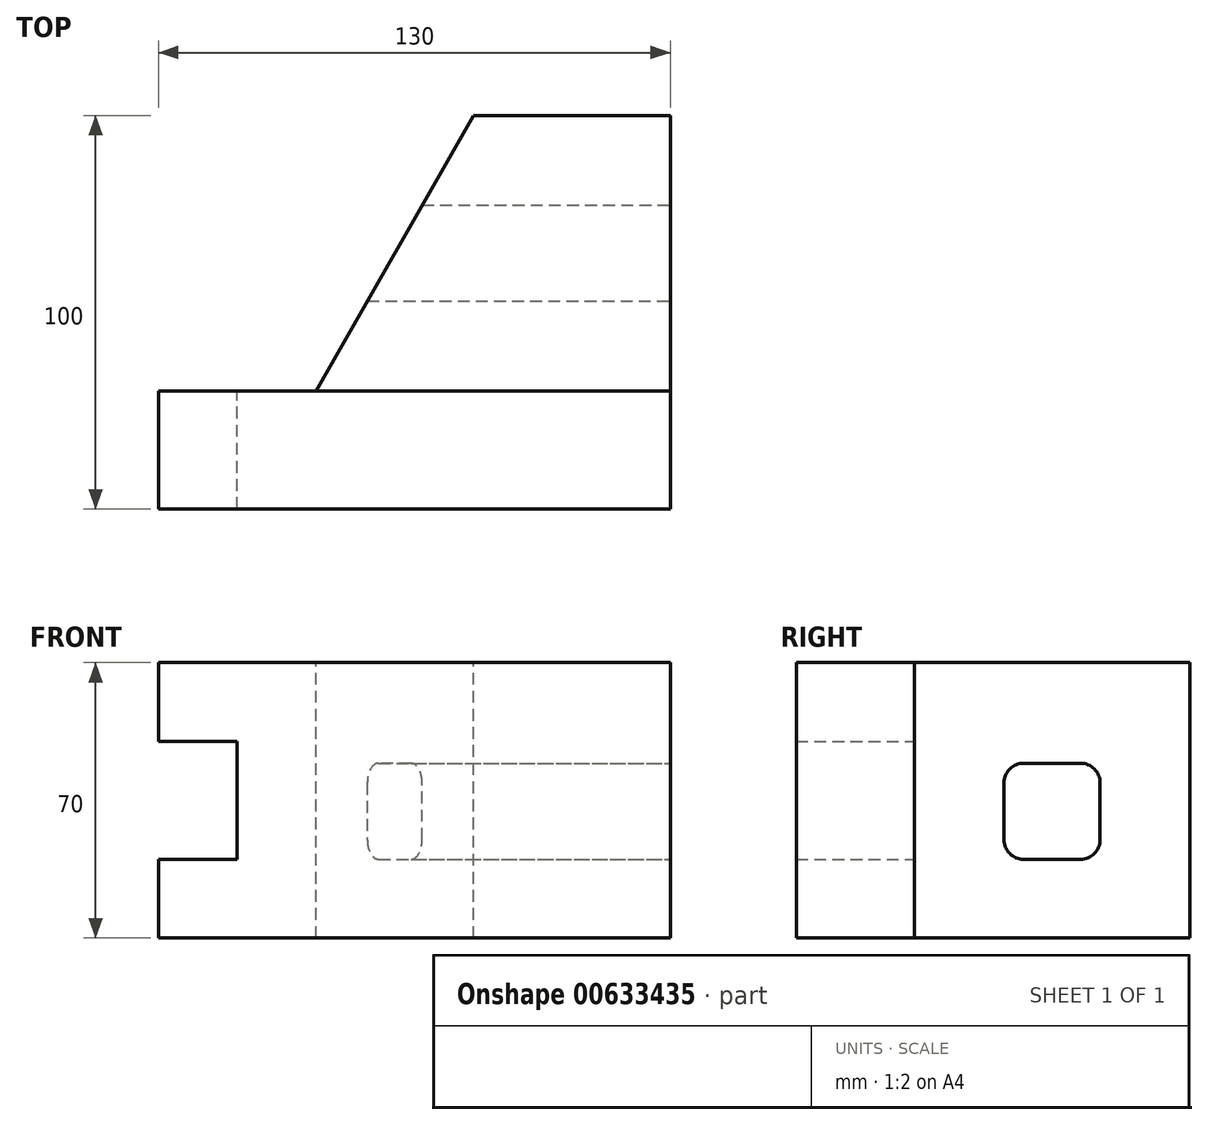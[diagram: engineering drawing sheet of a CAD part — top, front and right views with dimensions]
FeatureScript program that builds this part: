
annotation { "Feature Type Name" : "Feature", "Feature Type Description" : "" }
export const myFeature = defineFeature(function(context is Context, id is Id, definition is map)
    precondition{}
    {
        {
            var Q0;
            Q0=qCreatedBy(makeId("Front.planeOp"),FACE);
            var sketch = newSketch(context, id + "F0", { "sketchPlane" : qUnion([Q0])});
            skLineSegment(sketch, "E0.bottom", {"start": v(-88.85, 29.8) * mm, "end": v(41.15, 29.8) * mm});
            skLineSegment(sketch, "E0.top", {"start": v(-88.85, -40.2) * mm, "end": v(41.15, -40.2) * mm});
            skLineSegment(sketch, "E0.left", {"start": v(-88.85, 29.8) * mm, "end": v(-88.85, 9.8) * mm});
            skLineSegment(sketch, "E0.right", {"start": v(41.15, 29.8) * mm, "end": v(41.15, -40.2) * mm});
            skLineSegment(sketch, "E1", {"start": v(-88.85, 29.8) * mm, "end": v(-68.85, 29.8) * mm});
            skLineSegment(sketch, "E2", {"start": v(-68.85, -40.2) * mm, "end": v(-68.85, 29.8) * mm});
            skLineSegment(sketch, "E3", {"start": v(-68.85, 29.8) * mm, "end": v(-68.85, 9.8) * mm});
            skLineSegment(sketch, "E4", {"start": v(-68.85, 9.8) * mm, "end": v(-88.85, 9.8) * mm});
            skLineSegment(sketch, "E5", {"start": v(-88.85, -20.2) * mm, "end": v(-68.85, -20.2) * mm});
            skLineSegment(sketch, "E6.trimOffspring", {"start": v(-88.85, -20.2) * mm, "end": v(-88.85, -40.2) * mm});
            skSolve(sketch);
        }
        {
            var Q0;
            Q0 = qSketchRegion(id + "F0", true);
            extrude(context, id + "F1", {"entities" : qUnion([Q0]), "depth" : 30 * mm, "offsetDistance" : 25 * mm});
        }
        {
            var Q0;
            Q0=makeQuery(id+"F1.opExtrude","SWEPT_FACE",FACE,{"disambiguationData":[OSD([sQuery(id+"F0.wireOp",EDGE,"E0.bottom"),sQuery(id+"F0.wireOp",EDGE,"E1")])]});
            var sketch = newSketch(context, id + "F2", { "sketchPlane" : qUnion([Q0])});
            skLineSegment(sketch, "E7", {"start": v(41.15, 0) * mm, "end": v(41.15, 70) * mm});
            skLineSegment(sketch, "E8", {"start": v(41.15, 70) * mm, "end": v(-8.85, 70) * mm});
            skLineSegment(sketch, "E9", {"start": v(-88.85, 0) * mm, "end": v(-48.85, 0) * mm});
            skLineSegment(sketch, "E10", {"start": v(-48.85, 0) * mm, "end": v(-8.85, 70) * mm});
            skSolve(sketch);
        }
        {
            var Q0;
            {var subQ0=sQuery(id+"F2.wireOp",EDGE,"E7");Q0=makeQuery(id+"F2.imprint","IMPRINT",FACE,{"disambiguationData":[TD([[makeQuery(id+"F2.imprint","IMPRINT",EDGE,{"derivedFrom":subQ0}),1.0]])]});}
            extrude(context, id + "F3", {"entities" : qUnion([Q0]), "depth" : -70 * mm, "offsetDistance" : 25 * mm});
        }
        {
            var Q0;
            Q0=makeQuery(id+"F3.opExtrude","SWEPT_FACE",FACE,{"disambiguationData":[OSD([sQuery(id+"F2.wireOp",EDGE,"E7")])]});
            var sketch = newSketch(context, id + "F4", { "sketchPlane" : qUnion([Q0])});
            skLineSegment(sketch, "E11", {"start": v(22.8, -0.79) * mm, "end": v(22.8, -15.2) * mm});
            skLineSegment(sketch, "E12", {"start": v(27.8, -20.2) * mm, "end": v(42.2, -20.2) * mm});
            skLineSegment(sketch, "E13", {"start": v(47.2, -15.2) * mm, "end": v(47.2, -0.79) * mm});
            skLineSegment(sketch, "E14.top", {"start": v(42.2, -20.2) * mm, "end": v(27.8, -20.2) * mm});
            skLineSegment(sketch, "E14.left", {"start": v(47.2, -0.79) * mm, "end": v(47.2, -15.2) * mm});
            skPoint(sketch, "E15.orphan", {"position": v(47.2, -40.2) * mm});
            skPoint(sketch, "E16.orphan", {"position": v(70, -20.2) * mm});
            skPoint(sketch, "E17.orphan", {"position": v(22.8, -40.2) * mm});
            skPoint(sketch, "E18.start.orphan", {"position": v(22.8, 29.8) * mm});
            skPoint(sketch, "E19.orphan", {"position": v(0, -20.2) * mm});
            skLineSegment(sketch, "E20.bottom", {"start": v(42.2, 4.21) * mm, "end": v(27.8, 4.21) * mm});
            skPoint(sketch, "E21.visualSharp", {"position": v(47.2, 4.21) * mm});
            skArc(sketch, "E21.filletArc", {"start": v(47.2, -0.79) * mm, "mid": v(45.75, 2.75) * mm, "end": v(42.2, 4.21) * mm});
            skPoint(sketch, "E22.visualSharp", {"position": v(47.2, -20.2) * mm});
            skArc(sketch, "E22.filletArc", {"start": v(42.2, -20.2) * mm, "mid": v(45.75, -18.74) * mm, "end": v(47.2, -15.2) * mm});
            skPoint(sketch, "E23.visualSharp", {"position": v(22.8, -20.2) * mm});
            skArc(sketch, "E23.filletArc", {"start": v(22.8, -15.2) * mm, "mid": v(24.25, -18.74) * mm, "end": v(27.8, -20.2) * mm});
            skPoint(sketch, "E24.visualSharp", {"position": v(22.8, 4.21) * mm});
            skArc(sketch, "E24.filletArc", {"start": v(27.8, 4.21) * mm, "mid": v(24.25, 2.75) * mm, "end": v(22.8, -0.79) * mm});
            skSolve(sketch);
        }
        {
            var Q0;
            Q0 = qSketchRegion(id + "F4", true);
            extrude(context, id + "F5", {"entities" : qUnion([Q0]), "operationType" : NewBodyOperationType.REMOVE, "oppositeDirection" : true, "depth" : 1000 * mm, "offsetDistance" : 25 * mm});
        }
    });
